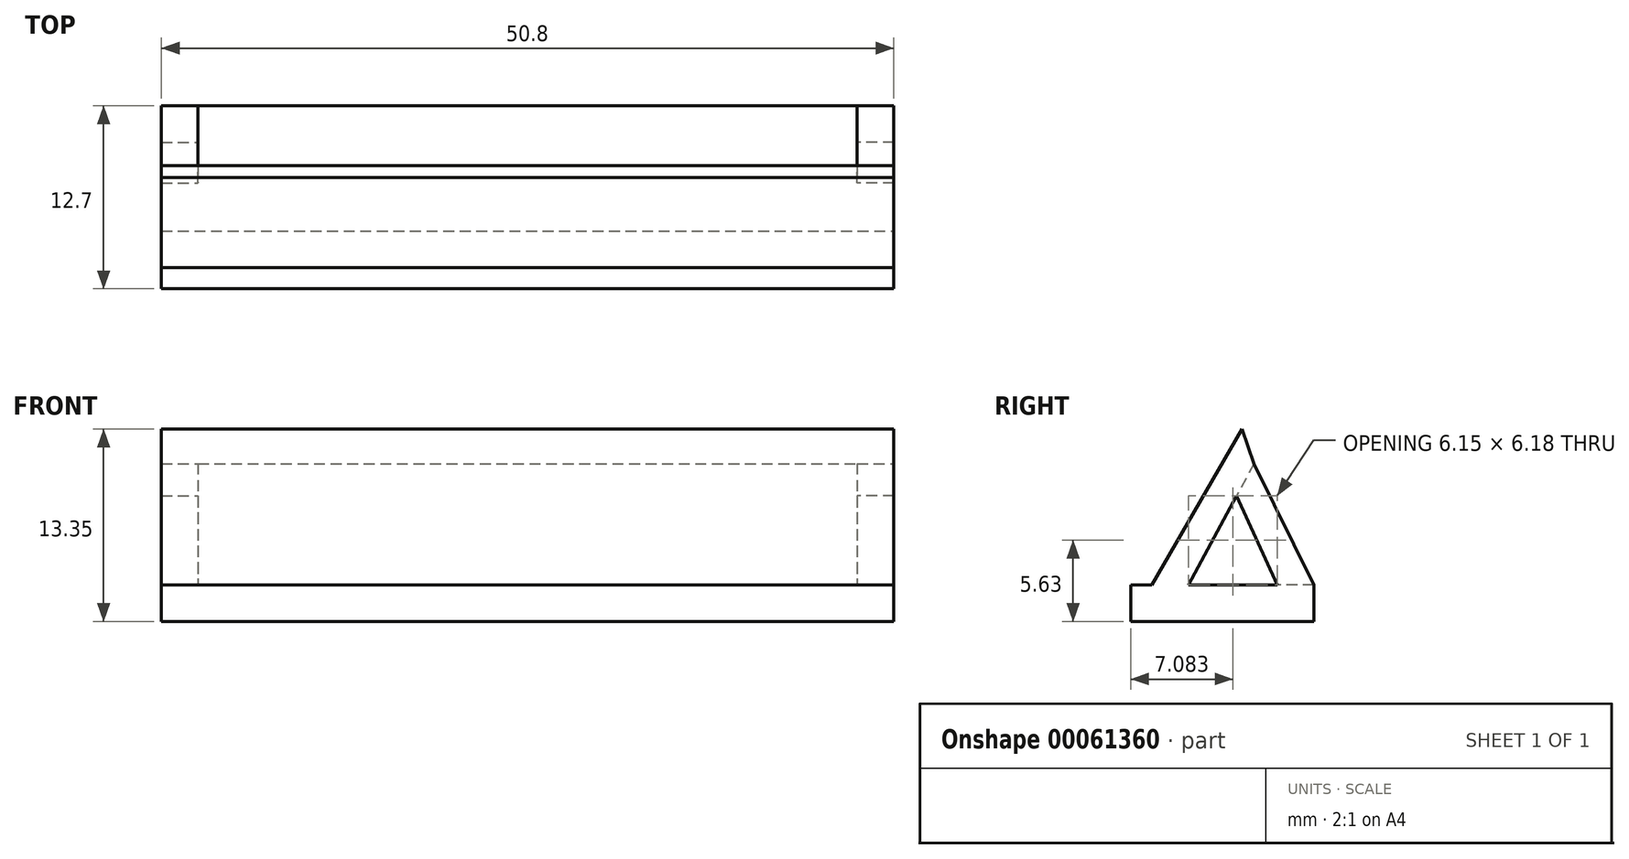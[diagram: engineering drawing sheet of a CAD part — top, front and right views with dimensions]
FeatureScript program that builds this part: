
annotation { "Feature Type Name" : "Feature", "Feature Type Description" : "" }
export const myFeature = defineFeature(function(context is Context, id is Id, definition is map)
    precondition{}
    {
        {
            var Q0;
            Q0=qCreatedBy(makeId("Top.planeOp"),FACE);
            var sketch = newSketch(context, id + "F0", { "sketchPlane" : qUnion([Q0])});
            skLineSegment(sketch, "E0.bottom", {"start": v(0, 0) * mm, "end": v(50.8, 0) * mm});
            skLineSegment(sketch, "E0.top", {"start": v(0, 12.7) * mm, "end": v(50.8, 12.7) * mm});
            skLineSegment(sketch, "E0.left", {"start": v(0, 0) * mm, "end": v(0, 12.7) * mm});
            skLineSegment(sketch, "E0.right", {"start": v(50.8, 0) * mm, "end": v(50.8, 12.7) * mm});
            skSolve(sketch);
        }
        {
            var Q0;
            Q0=qSketchRegion(id+"F0",true);
            extrude(context, id + "F1", {"entities" : qUnion([Q0]), "depth" : 2.54 * mm});
        }
        {
            var Q0;
            Q0=qCreatedBy(makeId("Right.planeOp"),FACE);
            var sketch = newSketch(context, id + "F2", { "sketchPlane" : qUnion([Q0])});
            skLineSegment(sketch, "E1", {"start": v(0, 0) * mm, "end": v(12.4, 0) * mm});
            skLineSegment(sketch, "E2", {"start": v(12.4, 0) * mm, "end": v(7.7, 13.35) * mm});
            skLineSegment(sketch, "E3", {"start": v(7.7, 13.35) * mm, "end": v(0, 0) * mm});
            skSolve(sketch);
        }
        {
            var Q0;
            Q0=qSketchRegion(id+"F2",true);
            extrude(context, id + "F3", {"entities" : qUnion([Q0]), "operationType" : NewBodyOperationType.ADD, "depth" : 50.8 * mm});
        }
        {
            var Q0;
            Q0=makeQuery(id+"F3.boolean.opBoolean","MERGE",FACE,{"derivedFrom":[makeQuery(id+"F1.opExtrude","SWEPT_FACE",FACE,{"disambiguationData":[OSD([sQuery(id+"F0.wireOp",EDGE,"E0.right")])]}),makeQuery(id+"F3.opExtrude","CAP_FACE",FACE,{"disambiguationData":[OSD([sQuery(id+"F2.wireOp",EDGE,"E1"),sQuery(id+"F2.wireOp",EDGE,"E2"),sQuery(id+"F2.wireOp",EDGE,"E3")])],"isStart":false})]});
            var sketch = newSketch(context, id + "F4", { "sketchPlane" : qUnion([Q0])});
            skLineSegment(sketch, "E4", {"start": v(1.47, 2.54) * mm, "end": v(11.5, 2.54) * mm});
            skLineSegment(sketch, "E5", {"start": v(11.5, 2.54) * mm, "end": v(7.7, 13.35) * mm});
            skLineSegment(sketch, "E6", {"start": v(7.7, 13.35) * mm, "end": v(1.47, 2.54) * mm});
            skLineSegment(sketch, "E7", {"start": v(1.47, 2.54) * mm, "end": v(1.47, 1.47) * mm});
            skLineSegment(sketch, "E8", {"start": v(1.47, 1.47) * mm, "end": v(4, 1.47) * mm});
            skLineSegment(sketch, "E9", {"start": v(4, 1.47) * mm, "end": v(4, 8.66) * mm});
            skLineSegment(sketch, "E10", {"start": v(7.7, 13.35) * mm, "end": v(9.84, 14.1) * mm});
            skLineSegment(sketch, "E11", {"start": v(9.84, 14.1) * mm, "end": v(10.68, 11.7) * mm});
            skLineSegment(sketch, "E12", {"start": v(10.68, 11.7) * mm, "end": v(7.73, 10.67) * mm});
            skLineSegment(sketch, "E13", {"start": v(8.55, 10.95) * mm, "end": v(4, 2.54) * mm});
            skSolve(sketch);
        }
        {
            var Q0;
            {var subQ6=sQuery(id+"F4.wireOp",EDGE,"E13");Q0=makeQuery(id+"F4.imprint","IMPRINT",FACE,{"disambiguationData":[TD([[makeQuery(id+"F4.imprint","IMPRINT",EDGE,{"derivedFrom":subQ6}),1.0]])]});}
            extrude(context, id + "F5", {"entities" : qUnion([Q0]), "operationType" : NewBodyOperationType.REMOVE, "oppositeDirection" : true, "depth" : 50.8 * mm});
        }
        {
            var Q0;
            Q0=makeQuery(id+"F3.boolean.opBoolean","MERGE",FACE,{"derivedFrom":[makeQuery(id+"F1.opExtrude","SWEPT_FACE",FACE,{"disambiguationData":[OSD([sQuery(id+"F0.wireOp",EDGE,"E0.right")])]}),makeQuery(id+"F3.opExtrude","CAP_FACE",FACE,{"disambiguationData":[OSD([sQuery(id+"F2.wireOp",EDGE,"E1"),sQuery(id+"F2.wireOp",EDGE,"E2"),sQuery(id+"F2.wireOp",EDGE,"E3")])],"isStart":false})]});
            var sketch = newSketch(context, id + "F6", { "sketchPlane" : qUnion([Q0])});
            skLineSegment(sketch, "E14", {"start": v(4, 2.54) * mm, "end": v(6.55, 2.54) * mm});
            skLineSegment(sketch, "E15", {"start": v(6.55, 2.54) * mm, "end": v(5.21, 4.78) * mm});
            skLineSegment(sketch, "E16", {"start": v(5.21, 4.78) * mm, "end": v(4, 2.54) * mm});
            skSolve(sketch);
        }
        {
            var Q0;
            Q0=qSketchRegion(id+"F6",true);
            extrude(context, id + "F7", {"entities" : qUnion([Q0]), "oppositeDirection" : true, "depth" : 50.8 * mm});
        }
        {
            var Q0;
            Q0=makeQuery(id+"F3.boolean.opBoolean","MERGE",FACE,{"derivedFrom":[makeQuery(id+"F1.opExtrude","SWEPT_FACE",FACE,{"disambiguationData":[OSD([sQuery(id+"F0.wireOp",EDGE,"E0.right")])]}),makeQuery(id+"F3.opExtrude","CAP_FACE",FACE,{"disambiguationData":[OSD([sQuery(id+"F2.wireOp",EDGE,"E1"),sQuery(id+"F2.wireOp",EDGE,"E2"),sQuery(id+"F2.wireOp",EDGE,"E3")])],"isStart":false})]});
            var sketch = newSketch(context, id + "F8", { "sketchPlane" : qUnion([Q0])});
            skCircle(sketch, "E17", {"center": v(4, 2.54) * mm, "radius": 0.78 * mm});
            skSolve(sketch);
        }
        {
            var Q0;
            Q0=qSketchRegion(id+"F8",true);
            extrude(context, id + "F9", {"entities" : qUnion([Q0]), "operationType" : NewBodyOperationType.ADD, "oppositeDirection" : true, "depth" : 25.4 * mm});
        }
        {
            var Q0;
            Q0=makeQuery(id+"F9.boolean.opBoolean","MERGE",FACE,{"derivedFrom":[makeQuery(id+"F3.boolean.opBoolean","MERGE",FACE,{"derivedFrom":[makeQuery(id+"F1.opExtrude","SWEPT_FACE",FACE,{"disambiguationData":[OSD([sQuery(id+"F0.wireOp",EDGE,"E0.right")])]}),makeQuery(id+"F3.opExtrude","CAP_FACE",FACE,{"disambiguationData":[OSD([sQuery(id+"F2.wireOp",EDGE,"E1"),sQuery(id+"F2.wireOp",EDGE,"E2"),sQuery(id+"F2.wireOp",EDGE,"E3")])],"isStart":false})]}),makeQuery(id+"F7.opExtrude","CAP_FACE",FACE,{"disambiguationData":[OSD([sQuery(id+"F6.wireOp",EDGE,"E14"),sQuery(id+"F6.wireOp",EDGE,"E15"),sQuery(id+"F6.wireOp",EDGE,"E16")])],"isStart":true}),makeQuery(id+"F9.opExtrude","CAP_FACE",FACE,{"disambiguationData":[OSD([sQuery(id+"F8.wireOp",EDGE,"E17")])],"isStart":true})]});
            var sketch = newSketch(context, id + "F10", { "sketchPlane" : qUnion([Q0])});
            skLineSegment(sketch, "E18", {"start": v(6.55, 2.54) * mm, "end": v(-2.97, 2.54) * mm});
            skLineSegment(sketch, "E19", {"start": v(5.21, 4.78) * mm, "end": v(2.12, -0.95) * mm});
            skLineSegment(sketch, "E20", {"start": v(6.55, 2.54) * mm, "end": v(5.21, 4.78) * mm});
            skSolve(sketch);
        }
        {
            var Q0;
            Q0=qSketchRegion(id+"F10",true);
            extrude(context, id + "F11", {"entities" : qUnion([Q0]), "operationType" : NewBodyOperationType.REMOVE, "oppositeDirection" : true, "depth" : 50.8 * mm});
        }
        {
            var Q0;
            {var subQ3=sQuery(id+"F0.wireOp",EDGE,"E0.left");var subQ4=sQuery(id+"F0.wireOp",EDGE,"E0.right");var subQ5=sQuery(id+"F0.wireOp",EDGE,"E0.top");Q0=makeQuery(id+"F11.boolean.opBoolean","MERGE",FACE,{"derivedFrom":[makeQuery(id+"F5.boolean.opBoolean","MERGE",FACE,{"derivedFrom":[makeQuery(id+"F3.boolean.opBoolean","SPLIT",FACE,{"disambiguationData":[TD([makeQuery(id+"F1.opExtrude","SWEPT_FACE",FACE,{"disambiguationData":[OSD([subQ5])]})])],"derivedFrom":makeQuery(id+"F1.opExtrude","CAP_FACE",FACE,{"disambiguationData":[OSD([sQuery(id+"F0.wireOp",EDGE,"E0.bottom"),subQ5,subQ3,subQ4])],"isStart":false})}),makeQuery(id+"F5.opExtrude","SWEPT_FACE",FACE,{"disambiguationData":[OSD([sQuery(id+"F4.wireOp",EDGE,"E4")])]})]}),makeQuery(id+"F11.opExtrude","SWEPT_FACE",FACE,{"disambiguationData":[OSD([sQuery(id+"F10.wireOp",EDGE,"E18")])]})]});}
            var sketch = newSketch(context, id + "F12", { "sketchPlane" : qUnion([Q0])});
            skLineSegment(sketch, "E21.bottom", {"start": v(50.8, 12.7) * mm, "end": v(48.26, 12.7) * mm});
            skLineSegment(sketch, "E21.top", {"start": v(50.8, 10.16) * mm, "end": v(48.26, 10.16) * mm});
            skLineSegment(sketch, "E21.left", {"start": v(50.8, 12.7) * mm, "end": v(50.8, 10.16) * mm});
            skLineSegment(sketch, "E21.right", {"start": v(48.26, 12.7) * mm, "end": v(48.26, 10.16) * mm});
            skLineSegment(sketch, "E22.bottom", {"start": v(0, 12.7) * mm, "end": v(2.54, 12.7) * mm});
            skLineSegment(sketch, "E22.top", {"start": v(0, 10.16) * mm, "end": v(2.54, 10.16) * mm});
            skLineSegment(sketch, "E22.left", {"start": v(0, 12.7) * mm, "end": v(0, 10.16) * mm});
            skLineSegment(sketch, "E22.right", {"start": v(2.54, 12.7) * mm, "end": v(2.54, 10.16) * mm});
            skSolve(sketch);
        }
        {
            var Q0;
            Q0=makeQuery(id+"F11.boolean.opBoolean","MERGE",FACE,{"derivedFrom":[makeQuery(id+"F5.boolean.opBoolean","COPY",FACE,{"derivedFrom":makeQuery(id+"F5.opExtrude","SWEPT_FACE",FACE,{"disambiguationData":[OSD([sQuery(id+"F4.wireOp",EDGE,"E13")])]})}),makeQuery(id+"F11.opExtrude","SWEPT_FACE",FACE,{"disambiguationData":[OSD([sQuery(id+"F10.wireOp",EDGE,"E19")])]})]});
            var sketch = newSketch(context, id + "F13", { "sketchPlane" : qUnion([Q0])});
            skLineSegment(sketch, "E23.bottom", {"start": v(-50.8, 13.7) * mm, "end": v(-48.26, 13.7) * mm});
            skLineSegment(sketch, "E23.top", {"start": v(-50.8, 11.16) * mm, "end": v(-48.26, 11.16) * mm});
            skLineSegment(sketch, "E23.left", {"start": v(-50.8, 13.7) * mm, "end": v(-50.8, 11.16) * mm});
            skLineSegment(sketch, "E23.right", {"start": v(-48.26, 13.7) * mm, "end": v(-48.26, 11.16) * mm});
            skLineSegment(sketch, "E24.bottom", {"start": v(0, 13.7) * mm, "end": v(-2.54, 13.7) * mm});
            skLineSegment(sketch, "E24.top", {"start": v(0, 11.16) * mm, "end": v(-2.54, 11.16) * mm});
            skLineSegment(sketch, "E24.left", {"start": v(0, 13.7) * mm, "end": v(0, 11.16) * mm});
            skLineSegment(sketch, "E24.right", {"start": v(-2.54, 13.7) * mm, "end": v(-2.54, 11.16) * mm});
            skSolve(sketch);
        }
        {
            var Q1;
            Q1=makeQuery(id+"F13.imprint","IMPRINT",FACE,{"disambiguationData":[TD([[makeQuery(id+"F13.imprint","IMPRINT",EDGE,{"derivedFrom":sQuery(id+"F13.wireOp",EDGE,"E23.bottom")}),1.0]])]});
            var Q2;
            Q2=makeQuery(id+"F12.imprint","IMPRINT",FACE,{"disambiguationData":[TD([[makeQuery(id+"F12.imprint","IMPRINT",EDGE,{"derivedFrom":sQuery(id+"F12.wireOp",EDGE,"E21.bottom")}),-1.0]])]});
            loft(context, id + "F14", {"operationType" : NewBodyOperationType.ADD, "sheetProfilesArray" : [{ "sheetProfileEntities" : qUnion([Q1]) }, { "sheetProfileEntities" : qUnion([Q2]) }]});
        }
        {
            var Q0;
            {var subQ3=sQuery(id+"F0.wireOp",EDGE,"E0.left");var subQ4=sQuery(id+"F0.wireOp",EDGE,"E0.right");var subQ5=sQuery(id+"F0.wireOp",EDGE,"E0.top");Q0=makeQuery(id+"F11.boolean.opBoolean","MERGE",FACE,{"derivedFrom":[makeQuery(id+"F5.boolean.opBoolean","MERGE",FACE,{"derivedFrom":[makeQuery(id+"F3.boolean.opBoolean","SPLIT",FACE,{"disambiguationData":[TD([makeQuery(id+"F1.opExtrude","SWEPT_FACE",FACE,{"disambiguationData":[OSD([subQ5])]})])],"derivedFrom":makeQuery(id+"F1.opExtrude","CAP_FACE",FACE,{"disambiguationData":[OSD([sQuery(id+"F0.wireOp",EDGE,"E0.bottom"),subQ5,subQ3,subQ4])],"isStart":false})}),makeQuery(id+"F5.opExtrude","SWEPT_FACE",FACE,{"disambiguationData":[OSD([sQuery(id+"F4.wireOp",EDGE,"E4")])]})]}),makeQuery(id+"F11.opExtrude","SWEPT_FACE",FACE,{"disambiguationData":[OSD([sQuery(id+"F10.wireOp",EDGE,"E18")])]})]});}
            var sketch = newSketch(context, id + "F15", { "sketchPlane" : qUnion([Q0])});
            skLineSegment(sketch, "E25.bottom", {"start": v(0, 12.7) * mm, "end": v(2.54, 12.7) * mm});
            skLineSegment(sketch, "E25.top", {"start": v(0, 10.16) * mm, "end": v(2.54, 10.16) * mm});
            skLineSegment(sketch, "E25.left", {"start": v(0, 12.7) * mm, "end": v(0, 10.16) * mm});
            skLineSegment(sketch, "E25.right", {"start": v(2.54, 12.7) * mm, "end": v(2.54, 10.16) * mm});
            skSolve(sketch);
        }
        {
            var Q0;
            Q0=makeQuery(id+"F11.boolean.opBoolean","MERGE",FACE,{"derivedFrom":[makeQuery(id+"F5.boolean.opBoolean","COPY",FACE,{"derivedFrom":makeQuery(id+"F5.opExtrude","SWEPT_FACE",FACE,{"disambiguationData":[OSD([sQuery(id+"F4.wireOp",EDGE,"E13")])]})}),makeQuery(id+"F11.opExtrude","SWEPT_FACE",FACE,{"disambiguationData":[OSD([sQuery(id+"F10.wireOp",EDGE,"E19")])]})]});
            var sketch = newSketch(context, id + "F16", { "sketchPlane" : qUnion([Q0])});
            skLineSegment(sketch, "E26.bottom", {"start": v(0, 13.7) * mm, "end": v(-2.54, 13.7) * mm});
            skLineSegment(sketch, "E26.top", {"start": v(0, 11.16) * mm, "end": v(-2.54, 11.16) * mm});
            skLineSegment(sketch, "E26.left", {"start": v(0, 13.7) * mm, "end": v(0, 11.16) * mm});
            skLineSegment(sketch, "E26.right", {"start": v(-2.54, 13.7) * mm, "end": v(-2.54, 11.16) * mm});
            skSolve(sketch);
        }
        {
            var Q1;
            Q1=makeQuery(id+"F16.imprint","IMPRINT",FACE,{"disambiguationData":[TD([[makeQuery(id+"F16.imprint","IMPRINT",EDGE,{"derivedFrom":sQuery(id+"F16.wireOp",EDGE,"E26.bottom")}),1.0]])]});
            var Q2;
            Q2=makeQuery(id+"F15.imprint","IMPRINT",FACE,{"disambiguationData":[TD([[makeQuery(id+"F15.imprint","IMPRINT",EDGE,{"derivedFrom":sQuery(id+"F15.wireOp",EDGE,"E25.bottom")}),-1.0]])]});
            loft(context, id + "F17", {"operationType" : NewBodyOperationType.ADD, "sheetProfilesArray" : [{ "sheetProfileEntities" : qUnion([Q1]) }, { "sheetProfileEntities" : qUnion([Q2]) }]});
        }
    });
